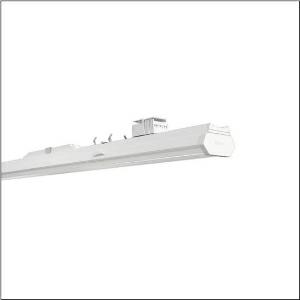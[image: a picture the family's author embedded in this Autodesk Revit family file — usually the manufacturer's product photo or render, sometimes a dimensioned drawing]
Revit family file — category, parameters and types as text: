
# Revit family: licross_r__11_protected_mo_51ts127n475f_3cb6
name_source: partatom
category: Lighting Fixtures
units: mm (PartAtom-declared; Revit-internal decimal feet)

## family parameters
Cut with Voids When Loaded = No
Host = Face
Light Source = No
Part Type = Normal
Room Calculation Point = No
Round Connector Dimension = Use Diameter
Shared = No

## types (1)
- Licross® 11 Protected MO (1 x LED, 7690 lm, 47.6 W, 4000K)
    Apparent Load = 48 VA
    CIE Flux Codes = 54 82 95 97 100
    Color Rendering = 80
    Color Temperature = 4000K
    Default Elevation = 1800 mm
    Description = Licross® 11 Protected MOluminaire insert, length: 1.500mm, width: 90mm, height: 101mm, LED rated luminous flux: 7.690lm, light colour: 840, control gear: ON/OFF, control gear: ECG, with plug, 3-pole, with phase selection, mains connection: 220..240V, AC, 50/60Hz, halogen-free wiring, primary optical cover: cover, of PMMA, light emission: direct with ceiling illumination distribution, protection rating (complete): IP50, insulation class (complete): insulation class I (protective earthing), certification: CE, ENEC, VDE, protection symbol: D if used in an environment with non-conductive dust loads with corresponding accessories, permissible ambient temperature for indoor applications: -35..+45°C, reducing of maximum allowable ambient temperature of 5°C with ceiling mounting, corresponds to IFS (International Featured Standards) requirements for safety and quality in the food industry, packaging unit: 1 piece
    Height = 92 mm
    Lamp = 1 x LED
    Lamp Light Flux = 7690 lm
    Lamp Power = 47.6 W
    Lamp count = 1
    Length = 1500 mm
    Luminous efficacy = 162 lm/W
    Manufacturer = Siteco
    ModVariant = No
    Model = 51TS127N475F
    Mounting Place = Ceiling
    Mounting Type = Pendant
    Number of Poles = 1
    OnlyDefault = Yes
    Power Factor = 1
    Product Name = Licross® 11 Protected MO
    Product group = luminaire insert
    ProductGroupID = 902
    Protection Class = Protection class I
    Protection Degree = IP 50
    RLX_Detail_Level = 1
    RlxData = <blob elided: 20433 chars, md5=a1987079>
    Socket = socket
    Standby Power = 0 W
    System Light Flux = 7690 lm
    System Power = 48 W
    Type Comments = Product without accessories
    Type Image = l_1256145.jpg
    URL = http://relux.com
    VarID = ---
    Voltage = 0 V
    Weight = 0.00 kg
    Width = 88 mm

## geometry (parser evidence)
native form markers: Blend x4, Sweep x11
no freeform markers — native parametric forms only
